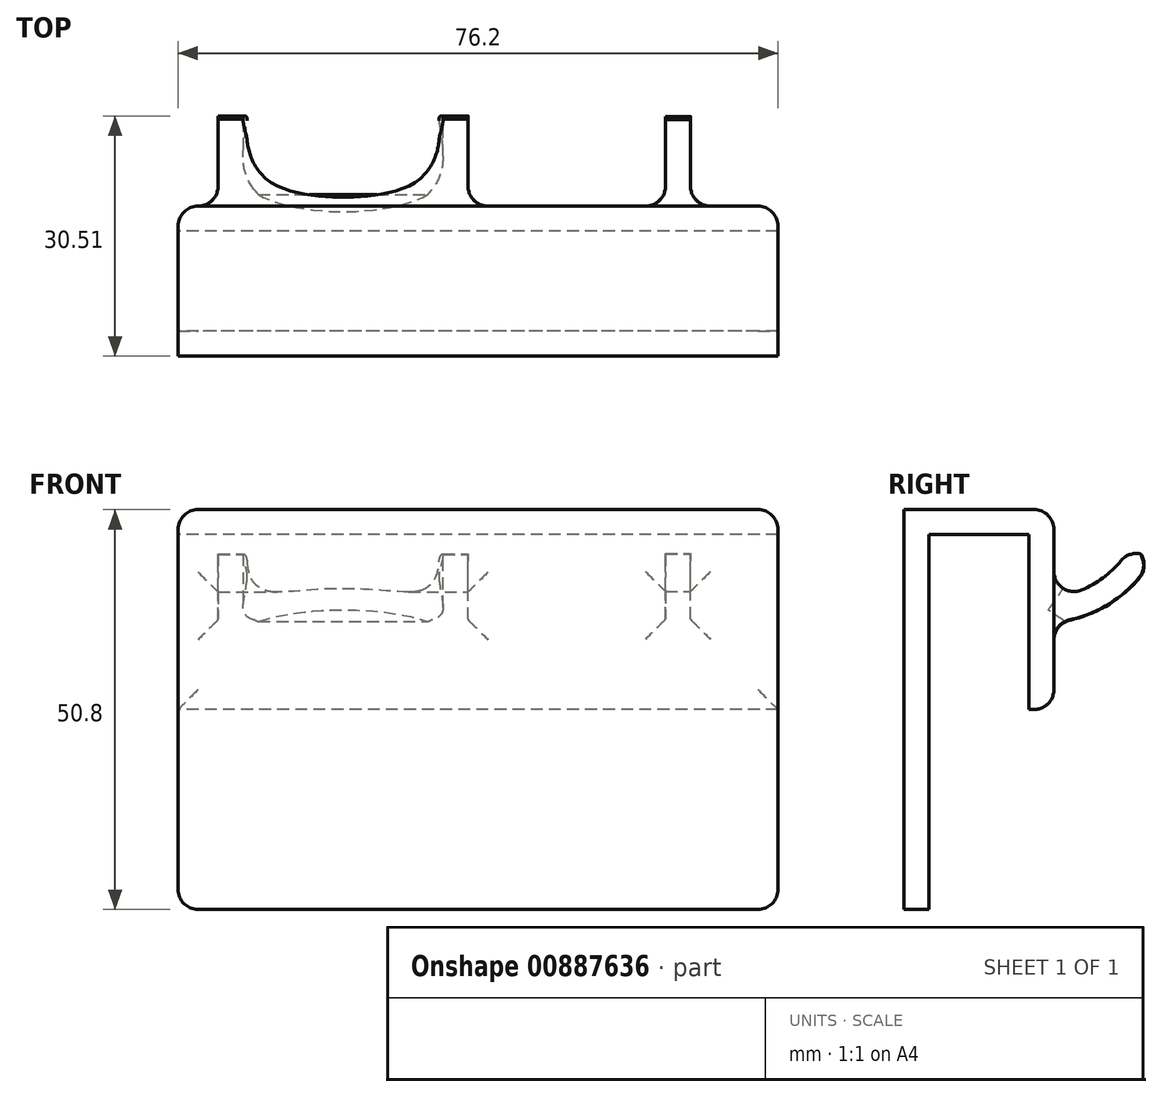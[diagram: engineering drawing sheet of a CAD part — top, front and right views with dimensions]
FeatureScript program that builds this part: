
annotation { "Feature Type Name" : "Feature", "Feature Type Description" : "" }
export const myFeature = defineFeature(function(context is Context, id is Id, definition is map)
    precondition{}
    {
        {
            var Q0;
            Q0=qCreatedBy(makeId("Right.planeOp"),FACE);
            var sketch = newSketch(context, id + "F0", { "sketchPlane" : qUnion([Q0])});
            skLineSegment(sketch, "E0", {"start": v(-3.18, 30.68) * mm, "end": v(-3.17, -20.12) * mm});
            skLineSegment(sketch, "E1", {"start": v(-3.17, -20.12) * mm, "end": v(0, -20.12) * mm});
            skLineSegment(sketch, "E2", {"start": v(0, -20.12) * mm, "end": v(0, 27.5) * mm});
            skLineSegment(sketch, "E3", {"start": v(0, 27.5) * mm, "end": v(12.7, 27.5) * mm});
            skLineSegment(sketch, "E4", {"start": v(12.7, 27.5) * mm, "end": v(12.7, 5.28) * mm});
            skLineSegment(sketch, "E5", {"start": v(12.7, 5.28) * mm, "end": v(15.87, 5.28) * mm});
            skLineSegment(sketch, "E6", {"start": v(15.87, 5.28) * mm, "end": v(15.87, 30.68) * mm});
            skLineSegment(sketch, "E7", {"start": v(-3.18, 30.68) * mm, "end": v(15.87, 30.68) * mm});
            skSolve(sketch);
        }
        {
            var Q0;
            Q0 = qSketchRegion(id + "F0", true);
            extrude(context, id + "F1", {"entities" : qUnion([Q0]), "depth" : 76.2 * mm, "offsetDistance" : 25.4 * mm});
        }
        {
            var Q0;
            Q0=makeQuery(id+"F1.opExtrude","SWEPT_FACE",FACE,{"disambiguationData":[OSD([sQuery(id+"F0.wireOp",EDGE,"E6")])]});
            var sketch = newSketch(context, id + "F2", { "sketchPlane" : qUnion([Q0])});
            skLineSegment(sketch, "E8.bottom", {"start": v(-61.91, 16.4) * mm, "end": v(-65.09, 16.4) * mm});
            skLineSegment(sketch, "E8.top", {"start": v(-61.91, 19.57) * mm, "end": v(-65.09, 19.57) * mm});
            skLineSegment(sketch, "E8.left", {"start": v(-61.91, 16.4) * mm, "end": v(-61.91, 19.57) * mm});
            skLineSegment(sketch, "E8.right", {"start": v(-65.09, 16.4) * mm, "end": v(-65.09, 19.57) * mm});
            skPoint(sketch, "E8.middle", {"position": v(-63.5, 17.98) * mm});
            skPoint(sketch, "E8.middle.positionSnap0", {"position": v(-76.2, 17.98) * mm});
            skPoint(sketch, "E8.centerSnap0", {"position": v(-76.2, 17.98) * mm});
            skSolve(sketch);
        }
        {
            var Q0;
            Q0=makeQuery(id+"F2.imprint","IMPRINT",FACE,{"disambiguationData":[TD([[makeQuery(id+"F2.imprint","IMPRINT",EDGE,{"derivedFrom":sQuery(id+"F2.wireOp",EDGE,"E8.bottom")}),1.0]])]});
            var sketch = newSketch(context, id + "F3", { "sketchPlane" : qUnion([Q0])});
            skLineSegment(sketch, "E9.bottom", {"start": v(-5.08, 16.34) * mm, "end": v(-36.83, 16.34) * mm});
            skLineSegment(sketch, "E9.top", {"start": v(-5.08, 19.51) * mm, "end": v(-36.83, 19.51) * mm});
            skLineSegment(sketch, "E9.left", {"start": v(-5.08, 16.34) * mm, "end": v(-5.08, 19.51) * mm});
            skLineSegment(sketch, "E9.right", {"start": v(-36.83, 16.34) * mm, "end": v(-36.83, 19.51) * mm});
            skPoint(sketch, "E9.middle", {"position": v(-20.96, 17.93) * mm});
            skSolve(sketch);
        }
        {
            var Q0;
            Q0=qCreatedBy(makeId("Right.planeOp"),FACE);
            var sketch = newSketch(context, id + "F4", { "sketchPlane" : qUnion([Q0])});
            skArc(sketch, "E10", {"start": v(13.34, 17.97) * mm, "mid": v(21.21, 19.6) * mm, "end": v(26.96, 25.22) * mm});
            skSolve(sketch);
        }
        {
            var Q0;
            Q0 = qSketchRegion(id + "F3", true);
            var Q1;
            Q1 = qConstructionFilter(qBodyType(qCreatedBy(id + "F4" ,EDGE), BodyType.WIRE), ConstructionObject.NO);
            sweep(context, id + "F5", {"operationType" : NewBodyOperationType.ADD, "profiles" : qUnion([Q0]), "path" : qUnion([Q1])});
        }
        {
            var Q0;
            Q0=makeQuery(id+"F2.imprint","IMPRINT",FACE,{"disambiguationData":[TD([[makeQuery(id+"F2.imprint","IMPRINT",EDGE,{"derivedFrom":sQuery(id+"F2.wireOp",EDGE,"E8.bottom")}),-1.0]])]});
            var Q1;
            Q1 = qConstructionFilter(qBodyType(qCreatedBy(id + "F4" ,EDGE), BodyType.WIRE), ConstructionObject.NO);
            sweep(context, id + "F6", {"operationType" : NewBodyOperationType.ADD, "profiles" : qUnion([Q0]), "path" : qUnion([Q1])});
        }
        {
            var Q0;
            Q0=makeQuery(id+"F1.opExtrude","SWEPT_FACE",FACE,{"disambiguationData":[OSD([sQuery(id+"F0.wireOp",EDGE,"E6")])]});
            var Q1;
            Q1=makeQuery(id+"F1.opExtrude","CAP_EDGE",EDGE,{"disambiguationData":[OSD([sQuery(id+"F0.wireOp",EDGE,"E1")])],"isStart":true});
            var Q2;
            Q2=makeQuery(id+"F1.opExtrude","CAP_EDGE",EDGE,{"disambiguationData":[OSD([sQuery(id+"F0.wireOp",EDGE,"E1")])],"isStart":false});
            var Q3;
            Q3=makeQuery(id+"F1.opExtrude","CAP_EDGE",EDGE,{"disambiguationData":[OSD([sQuery(id+"F0.wireOp",EDGE,"E7")])],"isStart":true});
            var Q4;
            Q4=makeQuery(id+"F1.opExtrude","CAP_EDGE",EDGE,{"disambiguationData":[OSD([sQuery(id+"F0.wireOp",EDGE,"E7")])],"isStart":false});
            fillet(context, id + "F7", {"entities" : qUnion([Q0, Q1, Q2, Q3, Q4]), "radius" : 2.54 * mm, "tangentPropagation" : true, "allowEdgeOverflow" : false});
        }
        {
            var Q0;
            Q0=makeQuery(id+"F5.opSweep","CAP_FACE",FACE,{"disambiguationData":[OSD([sQuery(id+"F3.wireOp",EDGE,"E9.bottom"),sQuery(id+"F3.wireOp",EDGE,"E9.top"),sQuery(id+"F3.wireOp",EDGE,"E9.left"),sQuery(id+"F3.wireOp",EDGE,"E9.right"),sQuery(id+"F66Ii9attYiJMfP_1.wireOp",VERTEX,"3HCx2po6-0TzL-L9mZ-c8hh-l2KRVatcYMYu.end")])],"isStart":false});
            var sketch = newSketch(context, id + "F8", { "sketchPlane" : qUnion([Q0])});
            skEllipse(sketch, "E11", {"center": v(20.96, 7.87) * mm, "majorRadius": 12.7 * mm, "minorRadius": 5.62 * mm, "majorAxis": v(-1, 0)});
            skPoint(sketch, "E11.centerSnap0", {"position": v(36.83, 7.87) * mm});
            skPoint(sketch, "E11.centerSnap1", {"position": v(20.96, 6.28) * mm});
            skSolve(sketch);
        }
        {
            var Q0;
            Q0 = qSketchRegion(id + "F8", true);
            extrude(context, id + "F9", {"entities" : qUnion([Q0]), "operationType" : NewBodyOperationType.REMOVE, "oppositeDirection" : true, "depth" : 12.7 * mm, "offsetDistance" : 25.4 * mm});
        }
        {
            var Q0;
            {var subQ0=sQuery(id+"F66Ii9attYiJMfP_1.wireOp",VERTEX,"3HCx2po6-0TzL-L9mZ-c8hh-l2KRVatcYMYu.end");var subQ1=sQuery(id+"F3.wireOp",EDGE,"E9.right");var subQ2=sQuery(id+"F3.wireOp",EDGE,"E9.top");var subQ3=sQuery(id+"F66Ii9attYiJMfP_1.wireOp",EDGE,"3HCx2po6-0TzL-L9mZ-c8hh-l2KRVatcYMYu");Q0=makeQuery(id+"F9.boolean.opBoolean","SPLIT",EDGE,{"disambiguationData":[TD([makeQuery(id+"F5.opSweep","SWEPT_FACE",FACE,{"disambiguationData":[OSD([subQ1,subQ3])]})])],"derivedFrom":makeQuery(id+"F5.opSweep","CAP_EDGE",EDGE,{"disambiguationData":[OSD([subQ2,subQ0])],"isStart":false})});}
            var Q1;
            {var subQ0=sQuery(id+"F66Ii9attYiJMfP_1.wireOp",VERTEX,"3HCx2po6-0TzL-L9mZ-c8hh-l2KRVatcYMYu.end");var subQ1=sQuery(id+"F3.wireOp",EDGE,"E9.left");var subQ2=sQuery(id+"F3.wireOp",EDGE,"E9.top");var subQ3=sQuery(id+"F66Ii9attYiJMfP_1.wireOp",EDGE,"3HCx2po6-0TzL-L9mZ-c8hh-l2KRVatcYMYu");Q1=makeQuery(id+"F9.boolean.opBoolean","SPLIT",EDGE,{"disambiguationData":[TD([makeQuery(id+"F5.opSweep","SWEPT_FACE",FACE,{"disambiguationData":[OSD([subQ1,subQ3])]})])],"derivedFrom":makeQuery(id+"F5.opSweep","CAP_EDGE",EDGE,{"disambiguationData":[OSD([subQ2,subQ0])],"isStart":false})});}
            var Q2;
            {var subQ0=sQuery(id+"F4.wireOp",VERTEX,"E10.end");var subQ1=sQuery(id+"F3.wireOp",EDGE,"E9.right");var subQ2=sQuery(id+"F3.wireOp",EDGE,"E9.bottom");var subQ3=sQuery(id+"F4.wireOp",EDGE,"E10");Q2=makeQuery(id+"F9.boolean.opBoolean","SPLIT",EDGE,{"disambiguationData":[TD([makeQuery(id+"F5.opSweep","SWEPT_FACE",FACE,{"disambiguationData":[OSD([subQ1,subQ3])]})])],"derivedFrom":makeQuery(id+"F5.opSweep","CAP_EDGE",EDGE,{"disambiguationData":[OSD([subQ2,subQ0])],"isStart":false})});}
            var Q3;
            {var subQ0=sQuery(id+"F4.wireOp",VERTEX,"E10.end");var subQ1=sQuery(id+"F3.wireOp",EDGE,"E9.left");var subQ2=sQuery(id+"F3.wireOp",EDGE,"E9.bottom");var subQ3=sQuery(id+"F4.wireOp",EDGE,"E10");Q3=makeQuery(id+"F9.boolean.opBoolean","SPLIT",EDGE,{"disambiguationData":[TD([makeQuery(id+"F5.opSweep","SWEPT_FACE",FACE,{"disambiguationData":[OSD([subQ1,subQ3])]})])],"derivedFrom":makeQuery(id+"F5.opSweep","CAP_EDGE",EDGE,{"disambiguationData":[OSD([subQ2,subQ0])],"isStart":false})});}
            fillet(context, id + "F10", {"entities" : qUnion([Q0, Q1, Q2, Q3]), "radius" : 2.54 * mm, "tangentPropagation" : true, "allowEdgeOverflow" : false});
        }
        {
            var Q0;
            Q0=makeQuery(id+"F6.opSweep","CAP_EDGE",EDGE,{"disambiguationData":[OSD([sQuery(id+"F2.wireOp",EDGE,"E8.top"),sQuery(id+"F4.wireOp",VERTEX,"E10.end")])],"isStart":false});
            var Q1;
            Q1=makeQuery(id+"F6.opSweep","CAP_EDGE",EDGE,{"disambiguationData":[OSD([sQuery(id+"F2.wireOp",EDGE,"E8.bottom"),sQuery(id+"F4.wireOp",VERTEX,"E10.end")])],"isStart":false});
            fillet(context, id + "F11", {"entities" : qUnion([Q0, Q1]), "radius" : 2.54 * mm, "tangentPropagation" : true, "allowEdgeOverflow" : false});
        }
    });
